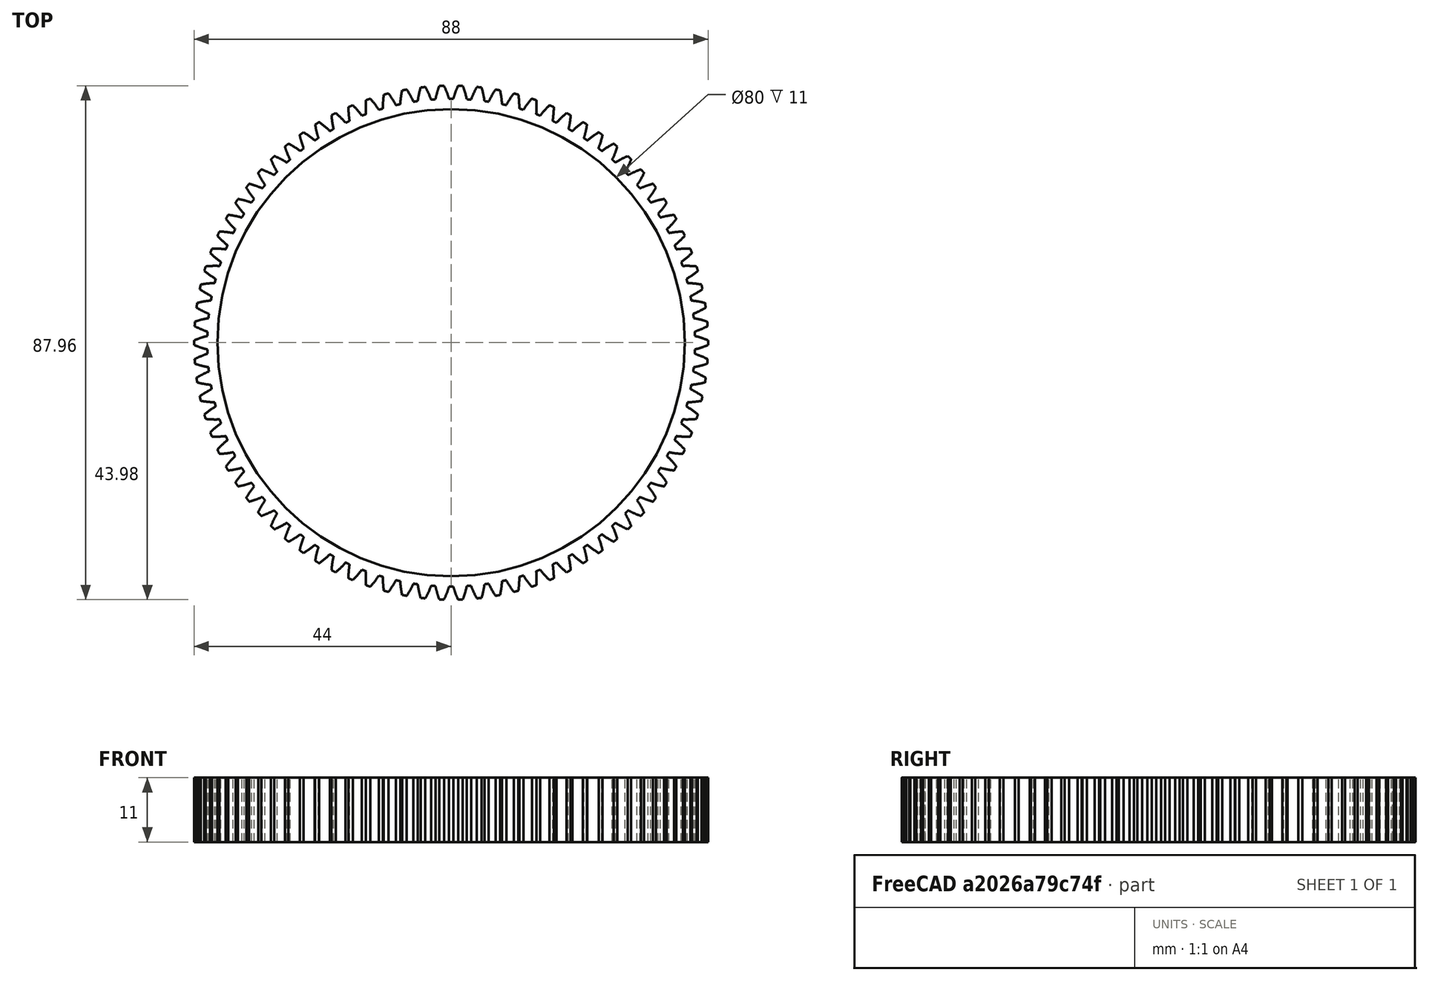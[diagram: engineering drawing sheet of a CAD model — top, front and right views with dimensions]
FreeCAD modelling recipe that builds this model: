
FCSTD DOCUMENT  (FreeCAD 0.19R24276 (Git))
Label: In_gear_t86
License: All rights reserved
LicenseURL: http://en.wikipedia.org/wiki/All_rights_reserved
objects: Sketcher::SketchObject×1, PartDesign::FeaturePython×1, PartDesign::Pocket×1, PartDesign::Body×1
note: 5 computed .brp shape members not serialized (recipe doc carries the construction recipe); baked Part::Feature solids carry a one-line shape summary decoded from their .brp

FEATURE [Sketcher::SketchObject] Sketch
  FullyConstrained = true
  MapMode = 5
  Support = -> [XY_Plane]
  sketch-geometry (1):
    g0: Circle CenterX=0 CenterY=0 CenterZ=0 NormalX=0 NormalY=0 NormalZ=1 AngleXU=0 Radius=40
  constraints (2):
    c: Coincident(g0,g-1)
    c: Diameter(g0) = 80
FEATURE [PartDesign::FeaturePython] involutegear  # WARN: FeaturePython — macro-defined, semantics opaque (R4)
  AttacherType = Attacher::AttachEngine3D
  backlash = 0
  beta = 0
  clearance = 0.25
  da = 88
  df = 83.5
  double_helix = false
  dw = 86
  head = 0
  height = 11
  module = 1
  numpoints = 6
  pressure_angle = 20
  properties_from_tool = false
  reversed_backlash = false
  shift = 0
  simple = false
  teeth = 86
  transverse_pitch = 3.14159
  undercut = false
  version = 0.0.3
FEATURE [PartDesign::Pocket] Pocket
  BaseFeature = -> involutegear
  Length = 5
  Length2 = 100
  Profile = -> Sketch
  Reversed = true
  Type = 1
FEATURE [PartDesign::Body] Body
  Group = -> [Sketch,involutegear,Pocket]
  Origin = -> Origin
  Tip = -> Pocket
